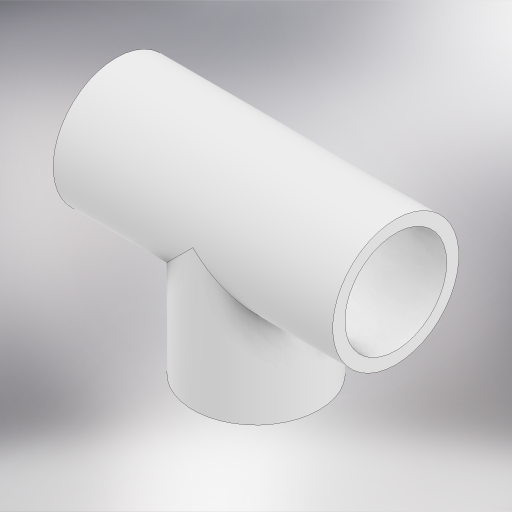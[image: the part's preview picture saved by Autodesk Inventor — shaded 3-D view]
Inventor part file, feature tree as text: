
AUTODESK INVENTOR PART (.ipt)
format: ipt  version: 2023 (Build 270158000, 158)  size: 301,056 bytes
history: native  units: in
note: dims shown in document units (in); Inventor stores cm internally (conversion verified against a paired STEP export)
features: extrude x4, sketch x4, other x1
ambient origin geometry x8: Origin, YZ Plane, XZ Plane, XY Plane, X Axis, Y Axis, Z Axis, Center Point
bodies: Body1 (feature_tree)
feature tree (9):
  other  "Sólido1"
  extrude  "Extrusión1"  Depth=1.4488in TaperAngle=0.0deg
  extrude  "Extrusión2"  Depth=2.8795in
  extrude  "Extrusión3"  Depth=2.8795in
  extrude  "Extrusión4"  [1 undecoded]
  sketch  "Boceto2"  dims[d0=1.2992in d1=1.4488in d2=0.0in]
  sketch  "Boceto3"  dims[d3=2.8795in d4=0.0in d5=1.0492in]
  sketch  "Boceto4"  dims[d6=2.8795in d7=0.0in d8=1.0492in]
  sketch  "Boceto5"  dims[d9=2.8795in d10=0.0in]
note: 1 required parameter value undecoded (feature->parameter linkage not recoverable at this tier; creation-order binding heuristic only, values carry confidence <= 0.55)
